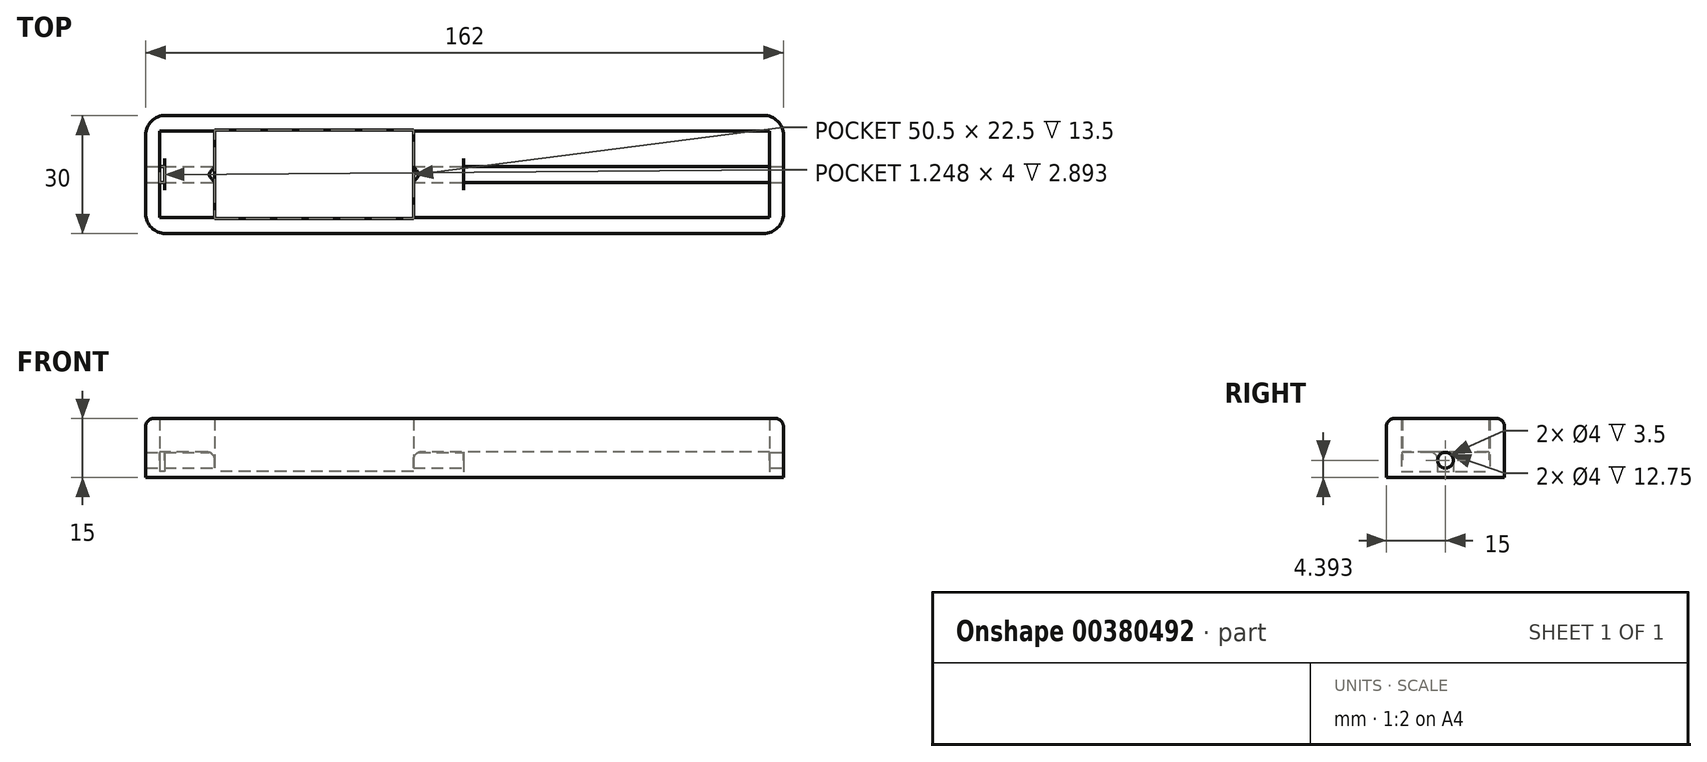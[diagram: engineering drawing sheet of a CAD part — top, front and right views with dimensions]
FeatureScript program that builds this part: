
annotation { "Feature Type Name" : "Feature", "Feature Type Description" : "" }
export const myFeature = defineFeature(function(context is Context, id is Id, definition is map)
    precondition{}
    {
        {
            var Q0;
            Q0=qCreatedBy(makeId("Top.planeOp"),FACE);
            var sketch = newSketch(context, id + "F0", { "sketchPlane" : qUnion([Q0])});
            skLineSegment(sketch, "E0.bottom", {"start": v(127.34, 15) * mm, "end": v(-34.66, 15) * mm});
            skLineSegment(sketch, "E0.top", {"start": v(127.34, -15) * mm, "end": v(-34.66, -15) * mm});
            skLineSegment(sketch, "E0.left", {"start": v(127.34, 15) * mm, "end": v(127.34, -15) * mm});
            skLineSegment(sketch, "E0.right", {"start": v(-34.66, 15) * mm, "end": v(-34.66, -15) * mm});
            skPoint(sketch, "E0.middle", {"position": v(46.34, 0) * mm});
            skLineSegment(sketch, "E1.bottom", {"start": v(123.84, 11) * mm, "end": v(-31.16, 11) * mm});
            skLineSegment(sketch, "E1.top", {"start": v(123.84, -11) * mm, "end": v(-31.16, -11) * mm});
            skLineSegment(sketch, "E1.left", {"start": v(123.84, 11) * mm, "end": v(123.84, -11) * mm});
            skLineSegment(sketch, "E1.right", {"start": v(-31.16, 11) * mm, "end": v(-31.16, -11) * mm});
            skLineSegment(sketch, "E2.bottom", {"start": v(33.33, -11.25) * mm, "end": v(-17.17, -11.25) * mm});
            skLineSegment(sketch, "E2.top", {"start": v(33.33, 11.25) * mm, "end": v(-17.17, 11.25) * mm});
            skLineSegment(sketch, "E2.left", {"start": v(33.33, -11.25) * mm, "end": v(33.33, 11.25) * mm});
            skLineSegment(sketch, "E2.right", {"start": v(-17.17, -11.25) * mm, "end": v(-17.17, 11.25) * mm});
            skPoint(sketch, "E2.middle", {"position": v(8.08, 0) * mm});
            skLineSegment(sketch, "E3.bottom", {"start": v(46.08, 11) * mm, "end": v(-29.92, 11) * mm});
            skLineSegment(sketch, "E3.top", {"start": v(46.08, -11) * mm, "end": v(-29.92, -11) * mm});
            skLineSegment(sketch, "E3.left", {"start": v(46.08, 11) * mm, "end": v(46.08, -11) * mm});
            skLineSegment(sketch, "E3.right", {"start": v(-29.92, 11) * mm, "end": v(-29.92, -11) * mm});
            skLineSegment(sketch, "E4.bottom", {"start": v(123.84, -2) * mm, "end": v(-31.16, -2) * mm});
            skLineSegment(sketch, "E4.top", {"start": v(123.84, 2) * mm, "end": v(-31.16, 2) * mm});
            skLineSegment(sketch, "E4.left", {"start": v(123.84, -2) * mm, "end": v(123.84, 2) * mm});
            skLineSegment(sketch, "E4.right", {"start": v(-31.16, -2) * mm, "end": v(-31.16, 2) * mm});
            skLineSegment(sketch, "E5", {"start": v(46.34, 0) * mm, "end": v(-34.66, 0) * mm});
            skSolve(sketch);
        }
        {
            var Q0;
            {var subQ0=sQuery(id+"F0.wireOp",EDGE,"E4.top");var subQ1=sQuery(id+"F0.wireOp",EDGE,"E2.left");var subQ2=makeQuery(id+"F0.imprint","INTERSECT",VERTEX,{"derivedFrom":[subQ1,subQ0]});Q0=makeQuery(id+"F0.imprint","IMPRINT",FACE,{"disambiguationData":[TD([[makeQuery(id+"F0.imprint","IMPRINT",EDGE,{"disambiguationData":[TD([[subQ2,-1.0]])],"derivedFrom":subQ1}),1.0]])]});}
            var Q1;
            {var subQ0=sQuery(id+"F0.wireOp",EDGE,"E5");var subQ1=sQuery(id+"F0.wireOp",EDGE,"E2.left");var subQ2=makeQuery(id+"F0.imprint","INTERSECT",VERTEX,{"derivedFrom":[subQ1,subQ0]});Q1=makeQuery(id+"F0.imprint","IMPRINT",FACE,{"disambiguationData":[TD([[makeQuery(id+"F0.imprint","IMPRINT",EDGE,{"disambiguationData":[TD([[subQ2,-1.0]])],"derivedFrom":subQ1}),1.0]])]});}
            var Q2;
            {var subQ0=sQuery(id+"F0.wireOp",EDGE,"E4.bottom");var subQ1=sQuery(id+"F0.wireOp",EDGE,"E2.left");var subQ2=makeQuery(id+"F0.imprint","INTERSECT",VERTEX,{"derivedFrom":[subQ1,subQ0]});Q2=makeQuery(id+"F0.imprint","IMPRINT",FACE,{"disambiguationData":[TD([[makeQuery(id+"F0.imprint","IMPRINT",EDGE,{"disambiguationData":[TD([[subQ2,-1.0]])],"derivedFrom":subQ1}),1.0]])]});}
            var Q3;
            {var subQ0=sQuery(id+"F0.wireOp",EDGE,"E4.bottom");var subQ1=sQuery(id+"F0.wireOp",EDGE,"E2.right");var subQ2=makeQuery(id+"F0.imprint","INTERSECT",VERTEX,{"derivedFrom":[subQ1,subQ0]});Q3=makeQuery(id+"F0.imprint","IMPRINT",FACE,{"disambiguationData":[TD([[makeQuery(id+"F0.imprint","IMPRINT",EDGE,{"disambiguationData":[TD([[subQ2,-1.0]])],"derivedFrom":subQ1}),1.0]])]});}
            var Q4;
            {var subQ0=sQuery(id+"F0.wireOp",EDGE,"E5");var subQ1=sQuery(id+"F0.wireOp",EDGE,"E2.right");var subQ2=makeQuery(id+"F0.imprint","INTERSECT",VERTEX,{"derivedFrom":[subQ1,subQ0]});Q4=makeQuery(id+"F0.imprint","IMPRINT",FACE,{"disambiguationData":[TD([[makeQuery(id+"F0.imprint","IMPRINT",EDGE,{"disambiguationData":[TD([[subQ2,-1.0]])],"derivedFrom":subQ1}),1.0]])]});}
            var Q5;
            {var subQ0=sQuery(id+"F0.wireOp",EDGE,"E5");var subQ1=sQuery(id+"F0.wireOp",EDGE,"E2.left");var subQ2=makeQuery(id+"F0.imprint","INTERSECT",VERTEX,{"derivedFrom":[subQ1,subQ0]});Q5=makeQuery(id+"F0.imprint","IMPRINT",FACE,{"disambiguationData":[TD([[makeQuery(id+"F0.imprint","IMPRINT",EDGE,{"disambiguationData":[TD([[subQ2,-1.0]])],"derivedFrom":subQ1}),-1.0]])]});}
            var Q6;
            {var subQ0=sQuery(id+"F0.wireOp",EDGE,"E4.bottom");var subQ1=sQuery(id+"F0.wireOp",EDGE,"E2.left");var subQ2=makeQuery(id+"F0.imprint","INTERSECT",VERTEX,{"derivedFrom":[subQ1,subQ0]});Q6=makeQuery(id+"F0.imprint","IMPRINT",FACE,{"disambiguationData":[TD([[makeQuery(id+"F0.imprint","IMPRINT",EDGE,{"disambiguationData":[TD([[subQ2,-1.0]])],"derivedFrom":subQ1}),-1.0]])]});}
            var Q7;
            {var subQ0=sQuery(id+"F0.wireOp",EDGE,"E4.left");Q7=makeQuery(id+"F0.imprint","IMPRINT",FACE,{"disambiguationData":[TD([[makeQuery(id+"F0.imprint","IMPRINT",EDGE,{"derivedFrom":subQ0}),1.0]])]});}
            var Q8;
            {var subQ0=sQuery(id+"F0.wireOp",EDGE,"E3.top");var subQ1=sQuery(id+"F0.wireOp",EDGE,"E2.left");var subQ2=makeQuery(id+"F0.imprint","INTERSECT",VERTEX,{"derivedFrom":[subQ1,subQ0]});Q8=makeQuery(id+"F0.imprint","IMPRINT",FACE,{"disambiguationData":[TD([[makeQuery(id+"F0.imprint","IMPRINT",EDGE,{"disambiguationData":[TD([[subQ2,-1.0]])],"derivedFrom":subQ1}),1.0]])]});}
            var Q9;
            {var subQ0=sQuery(id+"F0.wireOp",EDGE,"E2.top");Q9=makeQuery(id+"F0.imprint","IMPRINT",FACE,{"disambiguationData":[TD([[makeQuery(id+"F0.imprint","IMPRINT",EDGE,{"derivedFrom":subQ0}),1.0]])]});}
            var Q10;
            {var subQ0=sQuery(id+"F0.wireOp",EDGE,"E2.bottom");Q10=makeQuery(id+"F0.imprint","IMPRINT",FACE,{"disambiguationData":[TD([[makeQuery(id+"F0.imprint","IMPRINT",EDGE,{"derivedFrom":subQ0}),-1.0]])]});}
            var Q11;
            {var subQ0=sQuery(id+"F0.wireOp",EDGE,"E5");var subQ1=sQuery(id+"F0.wireOp",EDGE,"E3.right");var subQ2=makeQuery(id+"F0.imprint","INTERSECT",VERTEX,{"derivedFrom":[subQ1,subQ0]});Q11=makeQuery(id+"F0.imprint","IMPRINT",FACE,{"disambiguationData":[TD([[makeQuery(id+"F0.imprint","IMPRINT",EDGE,{"disambiguationData":[TD([[subQ2,-1.0]])],"derivedFrom":subQ1}),-1.0]])]});}
            var Q12;
            {var subQ0=sQuery(id+"F0.wireOp",EDGE,"E4.top");var subQ1=sQuery(id+"F0.wireOp",EDGE,"E3.right");var subQ2=makeQuery(id+"F0.imprint","INTERSECT",VERTEX,{"derivedFrom":[subQ1,subQ0]});Q12=makeQuery(id+"F0.imprint","IMPRINT",FACE,{"disambiguationData":[TD([[makeQuery(id+"F0.imprint","IMPRINT",EDGE,{"disambiguationData":[TD([[subQ2,-1.0]])],"derivedFrom":subQ1}),-1.0]])]});}
            extrude(context, id + "F1", {"entities" : qUnion([Q0, Q1, Q2, Q3, Q4, Q5, Q6, Q7, Q8, Q9, Q10, Q11, Q12]), "depth" : 1.5 * mm});
        }
        {
            var Q0;
            {var subQ0=sQuery(id+"F0.wireOp",EDGE,"E4.top");var subQ1=sQuery(id+"F0.wireOp",EDGE,"E2.right");var subQ2=makeQuery(id+"F0.imprint","INTERSECT",VERTEX,{"derivedFrom":[subQ1,subQ0]});Q0=makeQuery(id+"F0.imprint","IMPRINT",FACE,{"disambiguationData":[TD([[makeQuery(id+"F0.imprint","IMPRINT",EDGE,{"disambiguationData":[TD([[subQ2,-1.0]])],"derivedFrom":subQ1}),1.0]])]});}
            var Q1;
            {var subQ0=sQuery(id+"F0.wireOp",EDGE,"E1.right");var subQ1=sQuery(id+"F0.wireOp",EDGE,"E1.bottom");var subQ2=makeQuery(id+"F0.imprint","INTERSECT",VERTEX,{"derivedFrom":[subQ1,subQ0]});Q1=makeQuery(id+"F0.imprint","IMPRINT",FACE,{"disambiguationData":[TD([[makeQuery(id+"F0.imprint","IMPRINT",EDGE,{"disambiguationData":[TD([[subQ2,1.0]])],"derivedFrom":subQ1}),1.0]])]});}
            var Q2;
            {var subQ0=sQuery(id+"F0.wireOp",EDGE,"E3.top");var subQ1=sQuery(id+"F0.wireOp",EDGE,"E2.right");var subQ2=makeQuery(id+"F0.imprint","INTERSECT",VERTEX,{"derivedFrom":[subQ1,subQ0]});Q2=makeQuery(id+"F0.imprint","IMPRINT",FACE,{"disambiguationData":[TD([[makeQuery(id+"F0.imprint","IMPRINT",EDGE,{"disambiguationData":[TD([[subQ2,-1.0]])],"derivedFrom":subQ1}),1.0]])]});}
            var Q3;
            {var subQ0=sQuery(id+"F0.wireOp",EDGE,"E1.right");var subQ1=sQuery(id+"F0.wireOp",EDGE,"E1.top");var subQ2=makeQuery(id+"F0.imprint","INTERSECT",VERTEX,{"derivedFrom":[subQ1,subQ0]});Q3=makeQuery(id+"F0.imprint","IMPRINT",FACE,{"disambiguationData":[TD([[makeQuery(id+"F0.imprint","IMPRINT",EDGE,{"disambiguationData":[TD([[subQ2,1.0]])],"derivedFrom":subQ1}),-1.0]])]});}
            var Q4;
            {var subQ0=sQuery(id+"F0.wireOp",EDGE,"E3.top");var subQ1=sQuery(id+"F0.wireOp",EDGE,"E2.left");var subQ2=makeQuery(id+"F0.imprint","INTERSECT",VERTEX,{"derivedFrom":[subQ1,subQ0]});Q4=makeQuery(id+"F0.imprint","IMPRINT",FACE,{"disambiguationData":[TD([[makeQuery(id+"F0.imprint","IMPRINT",EDGE,{"disambiguationData":[TD([[subQ2,-1.0]])],"derivedFrom":subQ1}),-1.0]])]});}
            var Q5;
            {var subQ0=sQuery(id+"F0.wireOp",EDGE,"E4.top");var subQ1=sQuery(id+"F0.wireOp",EDGE,"E2.left");var subQ2=makeQuery(id+"F0.imprint","INTERSECT",VERTEX,{"derivedFrom":[subQ1,subQ0]});Q5=makeQuery(id+"F0.imprint","IMPRINT",FACE,{"disambiguationData":[TD([[makeQuery(id+"F0.imprint","IMPRINT",EDGE,{"disambiguationData":[TD([[subQ2,-1.0]])],"derivedFrom":subQ1}),-1.0]])]});}
            var Q6;
            {var subQ0=sQuery(id+"F0.wireOp",EDGE,"E1.left");var subQ1=sQuery(id+"F0.wireOp",EDGE,"E1.bottom");var subQ2=makeQuery(id+"F0.imprint","INTERSECT",VERTEX,{"derivedFrom":[subQ1,subQ0]});Q6=makeQuery(id+"F0.imprint","IMPRINT",FACE,{"disambiguationData":[TD([[makeQuery(id+"F0.imprint","IMPRINT",EDGE,{"disambiguationData":[TD([[subQ2,-1.0]])],"derivedFrom":subQ1}),1.0]])]});}
            var Q7;
            {var subQ0=sQuery(id+"F0.wireOp",EDGE,"E1.left");var subQ1=sQuery(id+"F0.wireOp",EDGE,"E1.top");var subQ2=makeQuery(id+"F0.imprint","INTERSECT",VERTEX,{"derivedFrom":[subQ1,subQ0]});Q7=makeQuery(id+"F0.imprint","IMPRINT",FACE,{"disambiguationData":[TD([[makeQuery(id+"F0.imprint","IMPRINT",EDGE,{"disambiguationData":[TD([[subQ2,-1.0]])],"derivedFrom":subQ1}),-1.0]])]});}
            extrude(context, id + "F2", {"entities" : qUnion([Q0, Q1, Q2, Q3, Q4, Q5, Q6, Q7]), "operationType" : NewBodyOperationType.ADD, "depth" : 6.5 * mm});
        }
        {
            var Q0;
            {var subQ24=sQuery(id+"F0.wireOp",EDGE,"E0.bottom");Q0=makeQuery(id+"F0.imprint","IMPRINT",FACE,{"disambiguationData":[TD([[makeQuery(id+"F0.imprint","IMPRINT",EDGE,{"derivedFrom":subQ24}),1.0]])]});}
            extrude(context, id + "F3", {"entities" : qUnion([Q0]), "operationType" : NewBodyOperationType.ADD, "depth" : 15 * mm});
        }
        {
            var Q0;
            Q0=makeQuery(id+"F3.opExtrude","SWEPT_FACE",FACE,{"disambiguationData":[OSD([sQuery(id+"F0.wireOp",EDGE,"E0.left")])]});
            var sketch = newSketch(context, id + "F4", { "sketchPlane" : qUnion([Q0])});
            skCircle(sketch, "E6", {"center": v(0, 4.4) * mm, "radius": 2 * mm});
            skPoint(sketch, "E6.centerSnap0", {"position": v(0, 0) * mm});
            skSolve(sketch);
        }
        {
            var Q0;
            Q0=makeQuery(id+"F4.imprint","IMPRINT",FACE,{"disambiguationData":[TD([[makeQuery(id+"F4.imprint","IMPRINT",EDGE,{"derivedFrom":sQuery(id+"F4.wireOp",EDGE,"E6")}),1.0]])]});
            extrude(context, id + "F5", {"entities" : qUnion([Q0]), "operationType" : NewBodyOperationType.REMOVE, "endBound" : BoundingType.THROUGH_ALL, "oppositeDirection" : true, "depth" : 25 * mm});
        }
        {
            var Q0;
            {var subQ0=sQuery(id+"F0.wireOp",EDGE,"E4.bottom");var subQ1=makeQuery(id+"F0.imprint","INTERSECT",VERTEX,{"derivedFrom":[sQuery(id+"F0.wireOp",EDGE,"E3.right"),subQ0]});Q0=makeQuery(id+"F2.opExtrude","CAP_EDGE",EDGE,{"disambiguationData":[OSD([subQ0]),TDD([makeQuery(id+"F0.imprint","IMPRINT",EDGE,{"disambiguationData":[TD([[makeQuery(id+"F0.imprint","INTERSECT",VERTEX,{"derivedFrom":[sQuery(id+"F0.wireOp",EDGE,"E2.right"),subQ0]}),-1.0]])],"derivedFrom":subQ0}),makeQuery(id+"F0.imprint","IMPRINT",EDGE,{"disambiguationData":[TD([[subQ1,-1.0]])],"derivedFrom":subQ0})])],"isStart":false});}
            var Q1;
            {var subQ0=sQuery(id+"F0.wireOp",EDGE,"E4.top");var subQ1=makeQuery(id+"F0.imprint","INTERSECT",VERTEX,{"derivedFrom":[sQuery(id+"F0.wireOp",EDGE,"E3.right"),subQ0]});Q1=makeQuery(id+"F2.opExtrude","CAP_EDGE",EDGE,{"disambiguationData":[OSD([subQ0]),TDD([makeQuery(id+"F0.imprint","IMPRINT",EDGE,{"disambiguationData":[TD([[makeQuery(id+"F0.imprint","INTERSECT",VERTEX,{"derivedFrom":[sQuery(id+"F0.wireOp",EDGE,"E2.right"),subQ0]}),-1.0]])],"derivedFrom":subQ0}),makeQuery(id+"F0.imprint","IMPRINT",EDGE,{"disambiguationData":[TD([[subQ1,-1.0]])],"derivedFrom":subQ0})])],"isStart":false});}
            var Q2;
            {var subQ0=sQuery(id+"F0.wireOp",EDGE,"E2.right");Q2=makeQuery(id+"F2.opExtrude","CAP_EDGE",EDGE,{"disambiguationData":[OSD([subQ0]),TDD([makeQuery(id+"F0.imprint","IMPRINT",EDGE,{"disambiguationData":[TD([[makeQuery(id+"F0.imprint","INTERSECT",VERTEX,{"derivedFrom":[subQ0,sQuery(id+"F0.wireOp",EDGE,"E3.top")]}),-1.0]])],"derivedFrom":subQ0})])],"isStart":false});}
            var Q3;
            {var subQ0=sQuery(id+"F0.wireOp",EDGE,"E2.right");Q3=makeQuery(id+"F2.opExtrude","CAP_EDGE",EDGE,{"disambiguationData":[OSD([subQ0]),TDD([makeQuery(id+"F0.imprint","IMPRINT",EDGE,{"disambiguationData":[TD([[makeQuery(id+"F0.imprint","INTERSECT",VERTEX,{"derivedFrom":[subQ0,sQuery(id+"F0.wireOp",EDGE,"E4.top")]}),-1.0]])],"derivedFrom":subQ0})])],"isStart":false});}
            var Q4;
            {var subQ0=sQuery(id+"F0.wireOp",EDGE,"E2.left");Q4=makeQuery(id+"F2.opExtrude","CAP_EDGE",EDGE,{"disambiguationData":[OSD([subQ0]),TDD([makeQuery(id+"F0.imprint","IMPRINT",EDGE,{"disambiguationData":[TD([[makeQuery(id+"F0.imprint","INTERSECT",VERTEX,{"derivedFrom":[subQ0,sQuery(id+"F0.wireOp",EDGE,"E4.top")]}),-1.0]])],"derivedFrom":subQ0})])],"isStart":false});}
            var Q5;
            {var subQ0=sQuery(id+"F0.wireOp",EDGE,"E2.left");Q5=makeQuery(id+"F2.opExtrude","CAP_EDGE",EDGE,{"disambiguationData":[OSD([subQ0]),TDD([makeQuery(id+"F0.imprint","IMPRINT",EDGE,{"disambiguationData":[TD([[makeQuery(id+"F0.imprint","INTERSECT",VERTEX,{"derivedFrom":[subQ0,sQuery(id+"F0.wireOp",EDGE,"E3.top")]}),-1.0]])],"derivedFrom":subQ0})])],"isStart":false});}
            var Q6;
            {var subQ0=sQuery(id+"F0.wireOp",EDGE,"E4.bottom");var subQ1=makeQuery(id+"F0.imprint","INTERSECT",VERTEX,{"derivedFrom":[sQuery(id+"F0.wireOp",EDGE,"E3.left"),subQ0]});Q6=makeQuery(id+"F2.opExtrude","CAP_EDGE",EDGE,{"disambiguationData":[OSD([subQ0]),TDD([makeQuery(id+"F0.imprint","IMPRINT",EDGE,{"disambiguationData":[TD([[subQ1,1.0]])],"derivedFrom":subQ0}),makeQuery(id+"F0.imprint","IMPRINT",EDGE,{"disambiguationData":[TD([[makeQuery(id+"F0.imprint","INTERSECT",VERTEX,{"derivedFrom":[sQuery(id+"F0.wireOp",EDGE,"E2.left"),subQ0]}),1.0]])],"derivedFrom":subQ0})])],"isStart":false});}
            var Q7;
            {var subQ0=sQuery(id+"F0.wireOp",EDGE,"E4.top");var subQ1=makeQuery(id+"F0.imprint","INTERSECT",VERTEX,{"derivedFrom":[sQuery(id+"F0.wireOp",EDGE,"E3.left"),subQ0]});Q7=makeQuery(id+"F2.opExtrude","CAP_EDGE",EDGE,{"disambiguationData":[OSD([subQ0]),TDD([makeQuery(id+"F0.imprint","IMPRINT",EDGE,{"disambiguationData":[TD([[subQ1,1.0]])],"derivedFrom":subQ0}),makeQuery(id+"F0.imprint","IMPRINT",EDGE,{"disambiguationData":[TD([[makeQuery(id+"F0.imprint","INTERSECT",VERTEX,{"derivedFrom":[sQuery(id+"F0.wireOp",EDGE,"E2.left"),subQ0]}),1.0]])],"derivedFrom":subQ0})])],"isStart":false});}
            var Q8;
            Q8=makeQuery(id+"F3.opExtrude","CAP_EDGE",EDGE,{"disambiguationData":[OSD([sQuery(id+"F0.wireOp",EDGE,"E0.bottom")])],"isStart":false});
            var Q9;
            Q9=makeQuery(id+"F3.opExtrude","CAP_EDGE",EDGE,{"disambiguationData":[OSD([sQuery(id+"F0.wireOp",EDGE,"E0.right")])],"isStart":false});
            var Q10;
            Q10=makeQuery(id+"F3.opExtrude","CAP_EDGE",EDGE,{"disambiguationData":[OSD([sQuery(id+"F0.wireOp",EDGE,"E0.top")])],"isStart":false});
            var Q11;
            Q11=makeQuery(id+"F3.opExtrude","CAP_EDGE",EDGE,{"disambiguationData":[OSD([sQuery(id+"F0.wireOp",EDGE,"E0.left")])],"isStart":false});
            fillet(context, id + "F6", {"entities" : qUnion([Q0, Q1, Q2, Q3, Q4, Q5, Q6, Q7, Q8, Q9, Q10, Q11]), "radius" : 2 * mm, "tangentPropagation" : true, "allowEdgeOverflow" : false});
        }
        {
            var Q0;
            Q0=makeQuery(id+"F3.opExtrude","SWEPT_EDGE",EDGE,{"disambiguationData":[OSD([sQuery(id+"F0.wireOp",EDGE,"E0.bottom"),sQuery(id+"F0.wireOp",EDGE,"E0.right")])]});
            var Q1;
            Q1=makeQuery(id+"F3.opExtrude","SWEPT_EDGE",EDGE,{"disambiguationData":[OSD([sQuery(id+"F0.wireOp",EDGE,"E0.top"),sQuery(id+"F0.wireOp",EDGE,"E0.right")])]});
            var Q2;
            Q2=makeQuery(id+"F3.opExtrude","SWEPT_EDGE",EDGE,{"disambiguationData":[OSD([sQuery(id+"F0.wireOp",EDGE,"E0.bottom"),sQuery(id+"F0.wireOp",EDGE,"E0.left")])]});
            var Q3;
            Q3=makeQuery(id+"F3.opExtrude","SWEPT_EDGE",EDGE,{"disambiguationData":[OSD([sQuery(id+"F0.wireOp",EDGE,"E0.top"),sQuery(id+"F0.wireOp",EDGE,"E0.left")])]});
            fillet(context, id + "F7", {"entities" : qUnion([Q0, Q1, Q2, Q3]), "radius" : 5 * mm, "tangentPropagation" : true, "allowEdgeOverflow" : false});
        }
    });
